# Revit family: HerzCon-Fan-coils and terminal units connection 90mm
name_source: partatom
category: Rohrzubehör
units: mm (PartAtom-declared; Revit-internal decimal feet)

## family parameters
Arbeitsebenenbasiert = Nein
Beim Laden mit Abzugskörper schneiden = Nein
Bemaßung runder Anschluss = Durchmesser verwenden
Gemeinsam genutzt = Nein
Immer vertikal = Ja
OmniClass-Nummer = 23.65.55.14
OmniClass-Titel = Valves for Liquid Services
Teiletyp = Unterbricht

## types (1)
- DN25
    Application = HerzCON has been designed to give a simple connection to fan-coils, or other terminal units, and utilises the HERZ 4006 SMART Pressure Independent Balancing Control Valve with HERZ multifunctional ball valve and a HERZ strainer with HERZ drain valve 2512.
On/off or modulating 0 – 10 V DC actuators can be fitted and integrated to a BMS if required.
The unit allows pressure independent control ensuring full stroke regardless of pressure fluctuations, while guaranteeing a constant flow rate to the terminal unit maximising energy efficiency for the system.
The HerzCON unit also permits flushing and isolating operations to be undertaken.
This means there is no product differentiation between heating and chilled, one unit does both applications.
The drain cock fitted to the strainer allows flushing without the need to remove the strainer basket and also allows the strainer basket to be cleaned in-situ.
    Body = dezincification-resistant brass
    D01 = 15 mm  [stored 0.0492126 ft]
    D02 = 27 mm
    D03 = 21.25 mm  [stored 0.0697178 ft]
    D04 = 15.5 mm  [stored 0.050853 ft]
    D05 = 33.8 mm
    D06 = 32.6 mm  [stored 0.106955 ft]
    D07 = 14.85 mm  [stored 0.0487205 ft]
    D08 = 19.1 mm
    D09 = 18.9 mm
    D10 = 13 mm
    D11 = 20 mm  [stored 0.0656168 ft]
    H01 = 39.5 mm
    H02 = 28 mm  [stored 0.0918635 ft]
    Hersteller = HERZ Armaturen Ges.m.b.H.
    Insulation box = EPP, water vapour impermeable, black
    L01 = 19.85 mm
    L02 = 4.8 mm  [stored 0.015748 ft]
    L03 = 18 mm
    L04 = 45 mm  [stored 0.147638 ft]
    L05 = 22 mm  [stored 0.0721785 ft]
    L06 = 20.5 mm  [stored 0.0672572 ft]
    L07 = 12.5 mm  [stored 0.0410105 ft]
    L08 = 14.75 mm
    L09 = 16 mm  [stored 0.0524934 ft]
    L10 = 25 mm  [stored 0.082021 ft]
    L11 = 14 mm  [stored 0.0459318 ft]
    Lift = 4 mm
    Max. differential pressure = 400000.0 Pa
    Max. operating pressure = 2500000.0 Pa
    Max. operating temperature = 130 °C
    Medium = Water purity in accordance with the ÖNORM H 5195 and VDI 2035 standards.
Ethylene and propylene glycol can be mixed to a ratio of 25 - 50 vol. [%].
    Membranes and O-rings = EPDM
    Min. operating temperature = -20 °C
    SCRNCODE = 05;04;04
    SCRNSEQ = ARM;TYP_ARM="DURR";02
    URL = www.herzvalves.com
    Vorgabe-Ansicht = 0 mm  [stored 0 ft]
    kvs-Wert (bypass funktion) = 10.00
    kvs-Wert (normal funktion) = 2.75

note: [stored X ft] marks values corroborated as IEEE doubles in the binary element streams (Revit-internal decimal feet)
